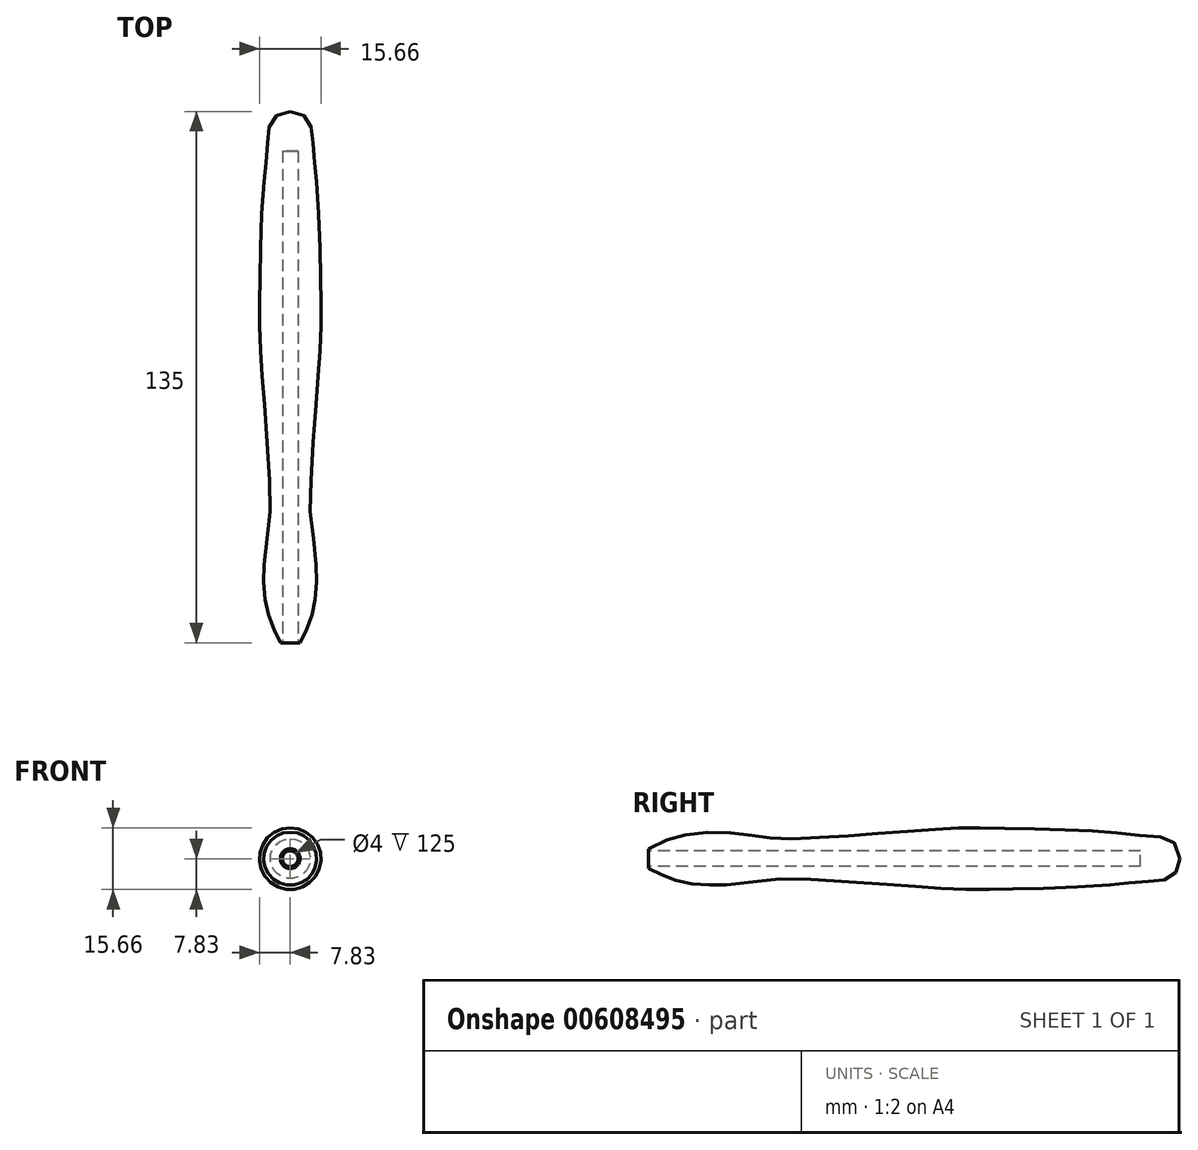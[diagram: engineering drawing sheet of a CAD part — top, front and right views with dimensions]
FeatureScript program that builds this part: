
annotation { "Feature Type Name" : "Feature", "Feature Type Description" : "" }
export const myFeature = defineFeature(function(context is Context, id is Id, definition is map)
    precondition{}
    {
        {
            var Q0;
            Q0=qCreatedBy(makeId("Right.planeOp"),FACE);
            var sketch = newSketch(context, id + "F0", { "sketchPlane" : qUnion([Q0])});
            skLineSegment(sketch, "E0", {"start": v(0, 0) * mm, "end": v(135, 0) * mm});
            skLineSegment(sketch, "E1", {"start": v(0, 0) * mm, "end": v(0, 2.5) * mm});
            skFitSpline(sketch, "E2", {"points": [v(0, 2.5) * mm, v(6.93, 5.51) * mm, v(15.94, 6.73) * mm, v(25.69, 6) * mm, v(32.62, 5.13) * mm, v(45.9, 5.51) * mm, v(62.95, 6.73) * mm, v(77.08, 7.7) * mm, v(85.96, 7.8) * mm, v(102.65, 7.46) * mm, v(116.78, 6.73) * mm, v(126.76, 5.75) * mm, v(133.1, 4.54) * mm, v(135, 0) * mm], "startDerivative": vector(132.84, 62.15) * mm, "endDerivative": vector(34.83, -113.91) * mm});
            skSolve(sketch);
        }
        {
            var Q0;
            Q0=makeQuery(id+"F0.imprint","IMPRINT",FACE,{"disambiguationData":[TD([[makeQuery(id+"F0.imprint","IMPRINT",EDGE,{"derivedFrom":sQuery(id+"F0.wireOp",EDGE,"E0")}),1.0]])]});
            var Q1;
            Q1=sQuery(id+"F0.wireOp",EDGE,"E0");
            revolve(context, id + "F1", {"entities" : qUnion([Q0]), "axis" : qUnion([Q1]), "revolveType" : RevolveType.FULL});
        }
        {
            var Q0;
            Q0=qCreatedBy(makeId("Front.planeOp"),FACE);
            var sketch = newSketch(context, id + "F2", { "sketchPlane" : qUnion([Q0])});
            skCircle(sketch, "E3", {"center": v(0, 0) * mm, "radius": 2 * mm});
            skSolve(sketch);
        }
        {
            var Q0;
            Q0 = qSketchRegion(id + "F2", true);
            extrude(context, id + "F3", {"entities" : qUnion([Q0]), "operationType" : NewBodyOperationType.REMOVE, "oppositeDirection" : true, "depth" : 125 * mm, "offsetDistance" : 25 * mm});
        }
    });
